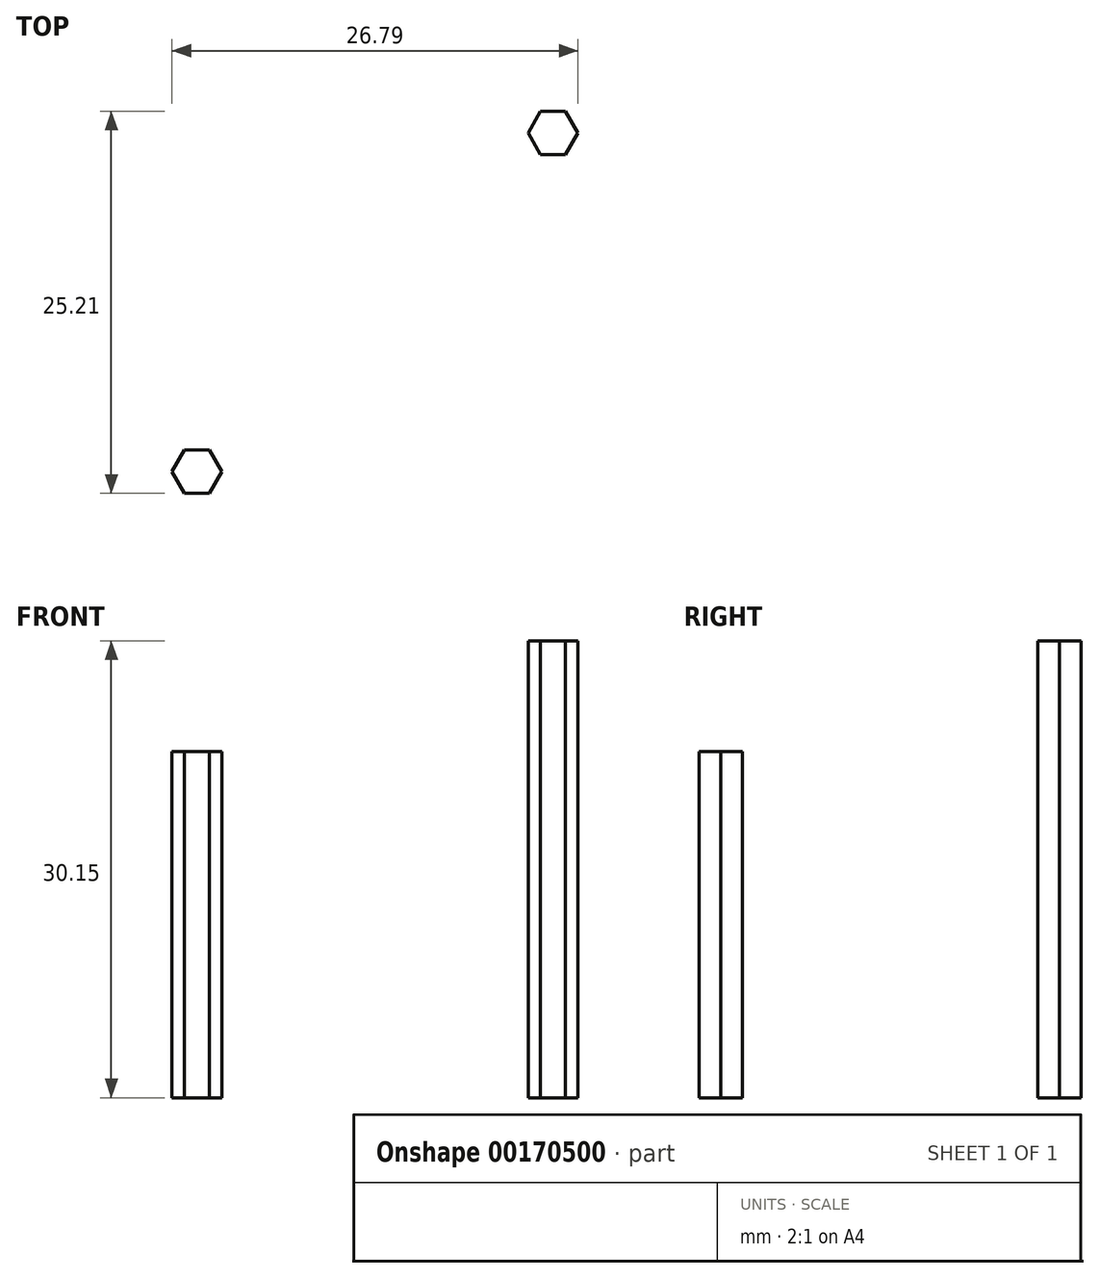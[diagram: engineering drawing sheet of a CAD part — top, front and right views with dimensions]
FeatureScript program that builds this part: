
annotation { "Feature Type Name" : "Feature", "Feature Type Description" : "" }
export const myFeature = defineFeature(function(context is Context, id is Id, definition is map)
    precondition{}
    {
        {
            var Q0;
            Q0=qCreatedBy(makeId("Top.planeOp"),FACE);
            var sketch = newSketch(context, id + "F0", { "sketchPlane" : qUnion([Q0])});
            skCircle(sketch, "E0.cCircle", {"center": v(0.53, 0.52) * mm, "radius": 1.42 * mm, "construction": true});
            skLineSegment(sketch, "E0.0", {"start": v(1.36, -0.9) * mm, "end": v(-0.29, -0.9) * mm});
            skLineSegment(sketch, "E0.1", {"start": v(-0.29, -0.9) * mm, "end": v(-1.1, 0.52) * mm});
            skLineSegment(sketch, "E0.2", {"start": v(-1.1, 0.52) * mm, "end": v(-0.29, 1.94) * mm});
            skLineSegment(sketch, "E0.3", {"start": v(-0.29, 1.94) * mm, "end": v(1.36, 1.94) * mm});
            skLineSegment(sketch, "E0.4", {"start": v(1.36, 1.94) * mm, "end": v(2.18, 0.52) * mm});
            skLineSegment(sketch, "E0.5", {"start": v(2.18, 0.52) * mm, "end": v(1.36, -0.9) * mm});
            skPoint(sketch, "E0.0.midPoint", {"position": v(0.53, -0.9) * mm});
            skSolve(sketch);
        }
        {
            var Q0;
            Q0=makeQuery(id+"F0.imprint","IMPRINT",FACE,{"disambiguationData":[TD([[makeQuery(id+"F0.imprint","IMPRINT",EDGE,{"derivedFrom":sQuery(id+"F0.wireOp",EDGE,"E0.0")}),-1.0]])]});
            extrude(context, id + "F1", {"entities" : qUnion([Q0]), "depth" : 30.15 * mm});
        }
        {
            var Q0;
            Q0=qCreatedBy(makeId("Top.planeOp"),FACE);
            var sketch = newSketch(context, id + "F2", { "sketchPlane" : qUnion([Q0])});
            skCircle(sketch, "E1.cCircle", {"center": v(-22.96, -21.84) * mm, "radius": 1.42 * mm, "construction": true});
            skLineSegment(sketch, "E1.0", {"start": v(-22.14, -23.27) * mm, "end": v(-23.79, -23.27) * mm});
            skLineSegment(sketch, "E1.1", {"start": v(-23.79, -23.27) * mm, "end": v(-24.6, -21.84) * mm});
            skLineSegment(sketch, "E1.2", {"start": v(-24.6, -21.84) * mm, "end": v(-23.79, -20.42) * mm});
            skLineSegment(sketch, "E1.3", {"start": v(-23.79, -20.42) * mm, "end": v(-22.14, -20.42) * mm});
            skLineSegment(sketch, "E1.4", {"start": v(-22.14, -20.42) * mm, "end": v(-21.32, -21.84) * mm});
            skLineSegment(sketch, "E1.5", {"start": v(-21.32, -21.84) * mm, "end": v(-22.14, -23.27) * mm});
            skPoint(sketch, "E1.0.midPoint", {"position": v(-22.96, -23.27) * mm});
            skSolve(sketch);
        }
        {
            var Q0;
            Q0=makeQuery(id+"F2.imprint","IMPRINT",FACE,{"disambiguationData":[TD([[makeQuery(id+"F2.imprint","IMPRINT",EDGE,{"derivedFrom":sQuery(id+"F2.wireOp",EDGE,"E1.0")}),-1.0]])]});
            extrude(context, id + "F3", {"entities" : qUnion([Q0]), "depth" : 22.86 * mm});
        }
    });
